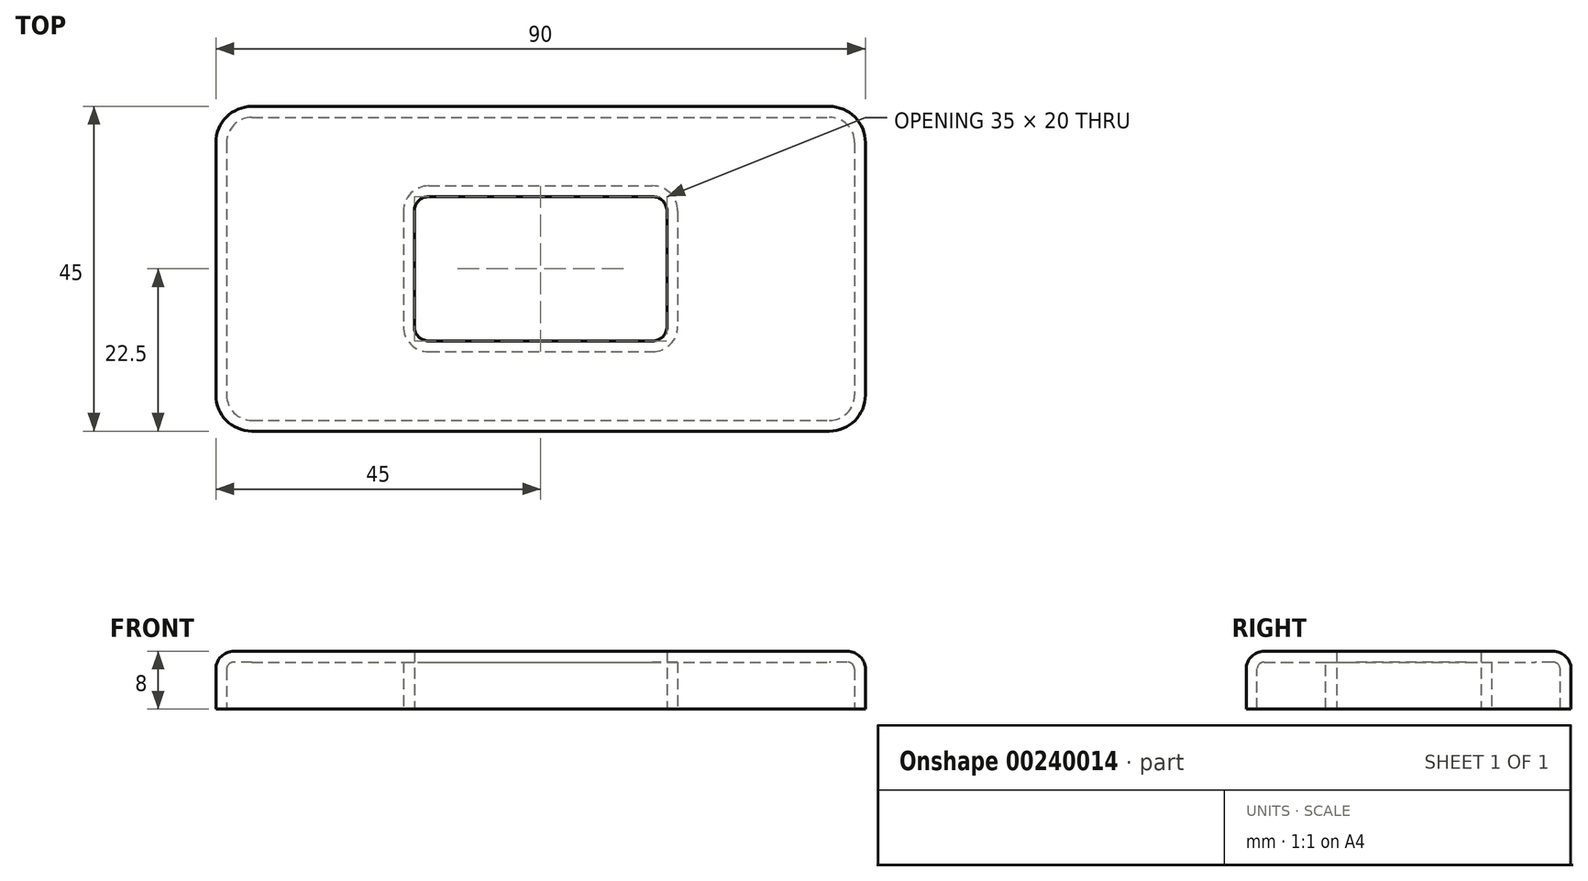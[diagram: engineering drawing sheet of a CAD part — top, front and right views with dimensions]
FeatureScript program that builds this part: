
annotation { "Feature Type Name" : "Feature", "Feature Type Description" : "" }
export const myFeature = defineFeature(function(context is Context, id is Id, definition is map)
    precondition{}
    {
        {
            var Q0;
            Q0=qCreatedBy(makeId("Top.planeOp"),FACE);
            var sketch = newSketch(context, id + "F0", { "sketchPlane" : qUnion([Q0])});
            skLineSegment(sketch, "E0.bottom", {"start": v(-40, 22.5) * mm, "end": v(40, 22.5) * mm});
            skLineSegment(sketch, "E0.top", {"start": v(-40, -22.5) * mm, "end": v(40, -22.5) * mm});
            skLineSegment(sketch, "E0.left", {"start": v(-45, 17.5) * mm, "end": v(-45, -17.5) * mm});
            skLineSegment(sketch, "E0.right", {"start": v(45, 17.5) * mm, "end": v(45, -17.5) * mm});
            skPoint(sketch, "E0.middle", {"position": v(0, 0) * mm});
            skPoint(sketch, "E1.visualSharp", {"position": v(-45, 22.5) * mm});
            skArc(sketch, "E1.filletArc", {"start": v(-40, 22.5) * mm, "mid": v(-43.54, 21.04) * mm, "end": v(-45, 17.5) * mm});
            skPoint(sketch, "E2.visualSharp", {"position": v(45, 22.5) * mm});
            skArc(sketch, "E2.filletArc", {"start": v(45, 17.5) * mm, "mid": v(43.54, 21.04) * mm, "end": v(40, 22.5) * mm});
            skPoint(sketch, "E3.visualSharp", {"position": v(45, -22.5) * mm});
            skArc(sketch, "E3.filletArc", {"start": v(40, -22.5) * mm, "mid": v(43.54, -21.04) * mm, "end": v(45, -17.5) * mm});
            skPoint(sketch, "E4.visualSharp", {"position": v(-45, -22.5) * mm});
            skArc(sketch, "E4.filletArc", {"start": v(-45, -17.5) * mm, "mid": v(-43.54, -21.04) * mm, "end": v(-40, -22.5) * mm});
            skLineSegment(sketch, "E5.bottom", {"start": v(-15.5, 10) * mm, "end": v(15.5, 10) * mm});
            skLineSegment(sketch, "E5.top", {"start": v(-15.5, -10) * mm, "end": v(15.5, -10) * mm});
            skLineSegment(sketch, "E5.left", {"start": v(-17.5, 8) * mm, "end": v(-17.5, -8) * mm});
            skLineSegment(sketch, "E5.right", {"start": v(17.5, 8) * mm, "end": v(17.5, -8) * mm});
            skPoint(sketch, "E6.visualSharp", {"position": v(-17.5, 10) * mm});
            skArc(sketch, "E6.filletArc", {"start": v(-15.5, 10) * mm, "mid": v(-16.91, 9.41) * mm, "end": v(-17.5, 8) * mm});
            skPoint(sketch, "E7.visualSharp", {"position": v(17.5, 10) * mm});
            skArc(sketch, "E7.filletArc", {"start": v(17.5, 8) * mm, "mid": v(16.91, 9.41) * mm, "end": v(15.5, 10) * mm});
            skPoint(sketch, "E8.visualSharp", {"position": v(17.5, -10) * mm});
            skArc(sketch, "E8.filletArc", {"start": v(15.5, -10) * mm, "mid": v(16.91, -9.41) * mm, "end": v(17.5, -8) * mm});
            skPoint(sketch, "E9.visualSharp", {"position": v(-17.5, -10) * mm});
            skArc(sketch, "E9.filletArc", {"start": v(-17.5, -8) * mm, "mid": v(-16.91, -9.41) * mm, "end": v(-15.5, -10) * mm});
            skSolve(sketch);
        }
        {
            var Q0;
            Q0=makeQuery(id+"F0.imprint","IMPRINT",FACE,{"disambiguationData":[TD([[makeQuery(id+"F0.imprint","IMPRINT",EDGE,{"derivedFrom":sQuery(id+"F0.wireOp",EDGE,"E0.bottom")}),-1.0]])]});
            extrude(context, id + "F1", {"entities" : qUnion([Q0]), "depth" : 8 * mm});
        }
        {
            var Q0;
            Q0=makeQuery(id+"F1.opExtrude","CAP_EDGE",EDGE,{"disambiguationData":[OSD([sQuery(id+"F0.wireOp",EDGE,"E0.top")])],"isStart":false});
            fillet(context, id + "F2", {"entities" : qUnion([Q0]), "radius" : 2.5 * mm, "tangentPropagation" : true, "allowEdgeOverflow" : false});
        }
        {
            var Q0;
            Q0=makeQuery(id+"F1.opExtrude","CAP_FACE",FACE,{"disambiguationData":[OSD([sQuery(id+"F0.wireOp",EDGE,"E0.bottom"),sQuery(id+"F0.wireOp",EDGE,"E0.top"),sQuery(id+"F0.wireOp",EDGE,"E0.left"),sQuery(id+"F0.wireOp",EDGE,"E0.right"),sQuery(id+"F0.wireOp",EDGE,"E1.filletArc"),sQuery(id+"F0.wireOp",EDGE,"E2.filletArc"),sQuery(id+"F0.wireOp",EDGE,"E3.filletArc"),sQuery(id+"F0.wireOp",EDGE,"E4.filletArc"),sQuery(id+"F0.wireOp",EDGE,"E5.bottom"),sQuery(id+"F0.wireOp",EDGE,"E5.top"),sQuery(id+"F0.wireOp",EDGE,"E5.left"),sQuery(id+"F0.wireOp",EDGE,"E5.right"),sQuery(id+"F0.wireOp",EDGE,"E6.filletArc"),sQuery(id+"F0.wireOp",EDGE,"E7.filletArc"),sQuery(id+"F0.wireOp",EDGE,"E8.filletArc"),sQuery(id+"F0.wireOp",EDGE,"E9.filletArc")])],"isStart":true});
            shell(context, id + "F3", {"entities" : qUnion([Q0]), "thickness" : 1.5 * mm});
        }
    });
